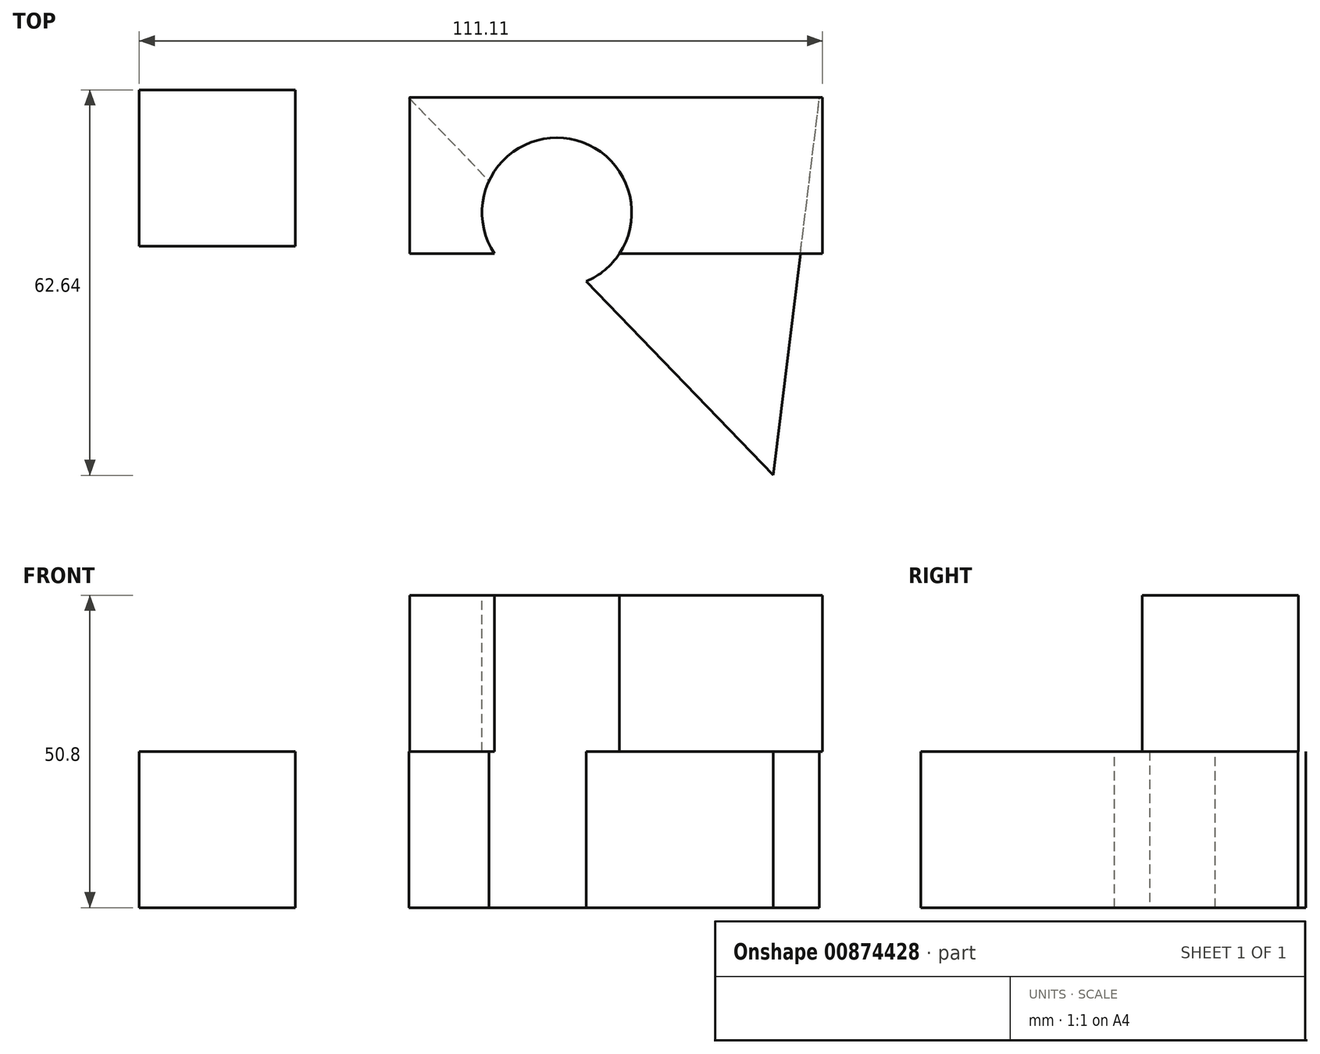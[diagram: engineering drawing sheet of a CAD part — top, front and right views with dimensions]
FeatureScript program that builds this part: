
annotation { "Feature Type Name" : "Feature", "Feature Type Description" : "" }
export const myFeature = defineFeature(function(context is Context, id is Id, definition is map)
    precondition{}
    {
        {
            var Q0;
            Q0=qCreatedBy(makeId("Top.planeOp"),FACE);
            var sketch = newSketch(context, id + "F0", { "sketchPlane" : qUnion([Q0])});
            skLineSegment(sketch, "E0.bottom", {"start": v(-70.78, 52.86) * mm, "end": v(-45.38, 52.86) * mm});
            skLineSegment(sketch, "E0.top", {"start": v(-70.78, 27.46) * mm, "end": v(-45.38, 27.46) * mm});
            skLineSegment(sketch, "E0.left", {"start": v(-70.78, 52.86) * mm, "end": v(-70.78, 27.46) * mm});
            skLineSegment(sketch, "E0.right", {"start": v(-45.38, 52.86) * mm, "end": v(-45.38, 27.46) * mm});
            skSolve(sketch);
        }
        {
            var Q0;
            Q0=makeQuery(id+"F0.imprint","IMPRINT",FACE,{"disambiguationData":[TD([[makeQuery(id+"F0.imprint","IMPRINT",EDGE,{"derivedFrom":sQuery(id+"F0.wireOp",EDGE,"E0.bottom")}),-1.0]])]});
            var Q1;
            Q1=sQuery(id+"F0.wireOp",EDGE,"E0.left");
            extrude(context, id + "F1", {"entities" : qUnion([Q0]), "surfaceEntities" : qUnion([Q1]), "depth" : 25.4 * mm, "offsetDistance" : 25.4 * mm});
        }
        {
            var Q0;
            Q0=makeQuery(id+"F1.opExtrude","CAP_FACE",FACE,{"disambiguationData":[OSD([sQuery(id+"F0.wireOp",EDGE,"E0.bottom"),sQuery(id+"F0.wireOp",EDGE,"E0.top"),sQuery(id+"F0.wireOp",EDGE,"E0.left"),sQuery(id+"F0.wireOp",EDGE,"E0.right")])],"isStart":false});
            var sketch = newSketch(context, id + "F2", { "sketchPlane" : qUnion([Q0])});
            skLineSegment(sketch, "E1.bottom", {"start": v(-26.8, 51.65) * mm, "end": v(40.33, 51.65) * mm});
            skLineSegment(sketch, "E1.top", {"start": v(-26.8, 26.25) * mm, "end": v(40.33, 26.25) * mm});
            skLineSegment(sketch, "E1.left", {"start": v(-26.8, 51.65) * mm, "end": v(-26.8, 26.25) * mm});
            skLineSegment(sketch, "E1.right", {"start": v(40.33, 51.65) * mm, "end": v(40.33, 26.25) * mm});
            skLineSegment(sketch, "E2.bottom", {"start": v(-14.89, 26.25) * mm, "end": v(32.33, 26.25) * mm});
            skLineSegment(sketch, "E2.top", {"start": v(-14.89, -10.38) * mm, "end": v(32.33, -10.38) * mm});
            skLineSegment(sketch, "E2.left", {"start": v(-14.89, 26.25) * mm, "end": v(-14.89, -10.38) * mm});
            skLineSegment(sketch, "E2.right", {"start": v(32.33, 26.25) * mm, "end": v(32.33, -10.38) * mm});
            skSolve(sketch);
        }
        {
            var Q0;
            Q0=makeQuery(id+"F2.imprint","IMPRINT",FACE,{"disambiguationData":[TD([[makeQuery(id+"F2.imprint","IMPRINT",EDGE,{"derivedFrom":sQuery(id+"F2.wireOp",EDGE,"E1.bottom")}),-1.0]])]});
            var Q1;
            Q1=makeQuery(id+"F2.imprint","IMPRINT",FACE,{"disambiguationData":[TD([[makeQuery(id+"F2.imprint","IMPRINT",EDGE,{"derivedFrom":sQuery(id+"F2.wireOp",EDGE,"E2.bottom")}),-1.0]])]});
            extrude(context, id + "F3", {"entities" : qUnion([Q0, Q1]), "depth" : 25.4 * mm, "offsetDistance" : 25.4 * mm});
        }
        {
            var Q0;
            Q0=qCreatedBy(makeId("Top.planeOp"),FACE);
            var sketch = newSketch(context, id + "F4", { "sketchPlane" : qUnion([Q0])});
            skLineSegment(sketch, "E3", {"start": v(-26.92, 51.59) * mm, "end": v(32.33, -9.78) * mm});
            skLineSegment(sketch, "E4", {"start": v(32.33, -9.78) * mm, "end": v(39.85, 51.59) * mm});
            skLineSegment(sketch, "E5", {"start": v(39.85, 51.59) * mm, "end": v(-26.92, 51.59) * mm});
            skSolve(sketch);
        }
        {
            var Q0;
            Q0=makeQuery(id+"F4.imprint","IMPRINT",FACE,{"disambiguationData":[TD([[makeQuery(id+"F4.imprint","IMPRINT",EDGE,{"derivedFrom":sQuery(id+"F4.wireOp",EDGE,"E3")}),1.0]])]});
            extrude(context, id + "F5", {"entities" : qUnion([Q0]), "operationType" : NewBodyOperationType.ADD, "depth" : 25.4 * mm, "offsetDistance" : 25.4 * mm});
        }
        {
            var Q0;
            Q0=makeQuery(id+"F3.opExtrude","CAP_FACE",FACE,{"disambiguationData":[OSD([sQuery(id+"F2.wireOp",EDGE,"E1.bottom"),sQuery(id+"F2.wireOp",EDGE,"E1.top"),sQuery(id+"F2.wireOp",EDGE,"E1.left"),sQuery(id+"F2.wireOp",EDGE,"E1.right"),sQuery(id+"F2.wireOp",EDGE,"E2.top"),sQuery(id+"F2.wireOp",EDGE,"E2.left"),sQuery(id+"F2.wireOp",EDGE,"E2.right")])],"isStart":false});
            var sketch = newSketch(context, id + "F6", { "sketchPlane" : qUnion([Q0])});
            skCircle(sketch, "E6", {"center": v(-2.86, 32.94) * mm, "radius": 12.17 * mm});
            skSolve(sketch);
        }
        {
            var Q0;
            Q0=makeQuery(id+"F6.imprint","IMPRINT",FACE,{"disambiguationData":[TD([[makeQuery(id+"F6.imprint","IMPRINT",EDGE,{"derivedFrom":sQuery(id+"F6.wireOp",EDGE,"E6")}),1.0]])]});
            var Q1;
            Q1 = qSketchRegion(id + "F8", true);
            extrude(context, id + "F7", {"entities" : qUnion([Q0, Q1]), "operationType" : NewBodyOperationType.REMOVE, "oppositeDirection" : true, "depth" : 152.4 * mm, "offsetDistance" : 25.4 * mm});
        }
    });
